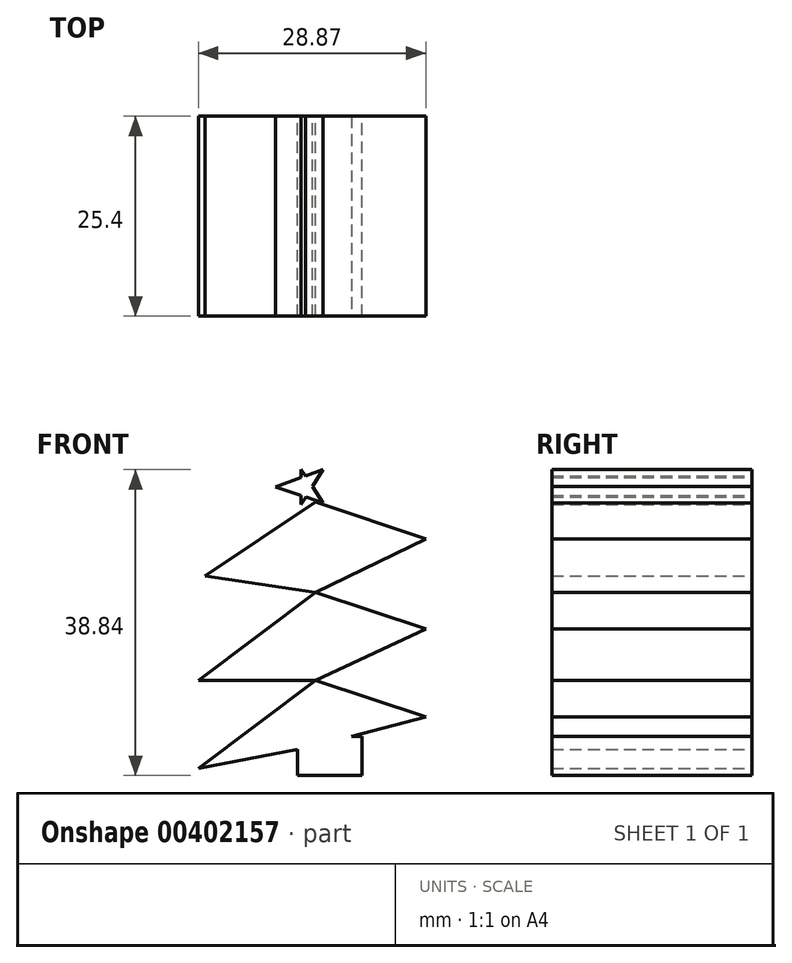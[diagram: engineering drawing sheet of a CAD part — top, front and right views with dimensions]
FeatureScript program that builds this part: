
annotation { "Feature Type Name" : "Feature", "Feature Type Description" : "" }
export const myFeature = defineFeature(function(context is Context, id is Id, definition is map)
    precondition{}
    {
        {
            var Q0;
            Q0=qCreatedBy(makeId("Front.planeOp"),FACE);
            var sketch = newSketch(context, id + "F0", { "sketchPlane" : qUnion([Q0])});
            skLineSegment(sketch, "E0", {"start": v(-3.52, 40.33) * mm, "end": v(-3.52, 9.34) * mm});
            skLineSegment(sketch, "E1", {"start": v(-3.52, 40.33) * mm, "end": v(10.46, 35.66) * mm});
            skLineSegment(sketch, "E2", {"start": v(10.46, 35.66) * mm, "end": v(-3.52, 28.86) * mm});
            skLineSegment(sketch, "E3", {"start": v(-3.52, 28.86) * mm, "end": v(10.46, 24.2) * mm});
            skLineSegment(sketch, "E4", {"start": v(10.46, 24.2) * mm, "end": v(-3.52, 17.69) * mm});
            skLineSegment(sketch, "E5", {"start": v(-3.52, 17.69) * mm, "end": v(10.46, 13.01) * mm});
            skLineSegment(sketch, "E6", {"start": v(10.46, 13.01) * mm, "end": v(-3.52, 9.34) * mm});
            skLineSegment(sketch, "E7", {"start": v(-3.52, 40.33) * mm, "end": v(-17.58, 30.91) * mm});
            skLineSegment(sketch, "E8", {"start": v(-17.58, 30.91) * mm, "end": v(-3.52, 28.86) * mm});
            skLineSegment(sketch, "E9", {"start": v(-3.52, 28.86) * mm, "end": v(-18.41, 17.7) * mm});
            skLineSegment(sketch, "E10", {"start": v(-18.41, 17.7) * mm, "end": v(-3.52, 17.69) * mm});
            skLineSegment(sketch, "E11", {"start": v(-3.52, 17.69) * mm, "end": v(-18.41, 6.51) * mm});
            skLineSegment(sketch, "E12", {"start": v(-18.41, 6.51) * mm, "end": v(-3.52, 9.34) * mm});
            skSolve(sketch);
        }
        {
            var Q0;
            Q0 = qSketchRegion(id + "F0", true);
            extrude(context, id + "F1", {"entities" : qUnion([Q0]), "depth" : 25.4 * mm});
        }
        {
            var Q0;
            Q0=qCreatedBy(makeId("Front.planeOp"),FACE);
            var sketch = newSketch(context, id + "F2", { "sketchPlane" : qUnion([Q0])});
            skLineSegment(sketch, "E13.bottom", {"start": v(-5.85, 10.53) * mm, "end": v(2.34, 10.53) * mm});
            skLineSegment(sketch, "E13.top", {"start": v(-5.85, 5.61) * mm, "end": v(2.34, 5.61) * mm});
            skLineSegment(sketch, "E13.left", {"start": v(-5.85, 10.53) * mm, "end": v(-5.85, 5.61) * mm});
            skLineSegment(sketch, "E13.right", {"start": v(2.34, 10.53) * mm, "end": v(2.34, 5.61) * mm});
            skSolve(sketch);
        }
        {
            var Q0;
            Q0 = qSketchRegion(id + "F2", true);
            extrude(context, id + "F3", {"entities" : qUnion([Q0]), "operationType" : NewBodyOperationType.ADD, "depth" : 25.4 * mm});
        }
        {
            var Q0;
            Q0=qCreatedBy(makeId("Front.planeOp"),FACE);
            var sketch = newSketch(context, id + "F4", { "sketchPlane" : qUnion([Q0])});
            skLineSegment(sketch, "E14", {"start": v(-5.38, 40) * mm, "end": v(-5.38, 44.45) * mm});
            skLineSegment(sketch, "E15", {"start": v(-5.38, 44.45) * mm, "end": v(-2.57, 40.24) * mm});
            skLineSegment(sketch, "E16", {"start": v(-2.57, 40.24) * mm, "end": v(-8.66, 42.23) * mm});
            skPoint(sketch, "E16.endSnap0", {"position": v(-5.38, 42.23) * mm});
            skLineSegment(sketch, "E17", {"start": v(-8.66, 42.23) * mm, "end": v(-2.57, 44.45) * mm});
            skLineSegment(sketch, "E18", {"start": v(-2.57, 44.45) * mm, "end": v(-5.38, 40) * mm});
            skSolve(sketch);
        }
        {
            var Q0;
            Q0 = qSketchRegion(id + "F4", true);
            extrude(context, id + "F5", {"entities" : qUnion([Q0]), "depth" : 25.4 * mm});
        }
    });
